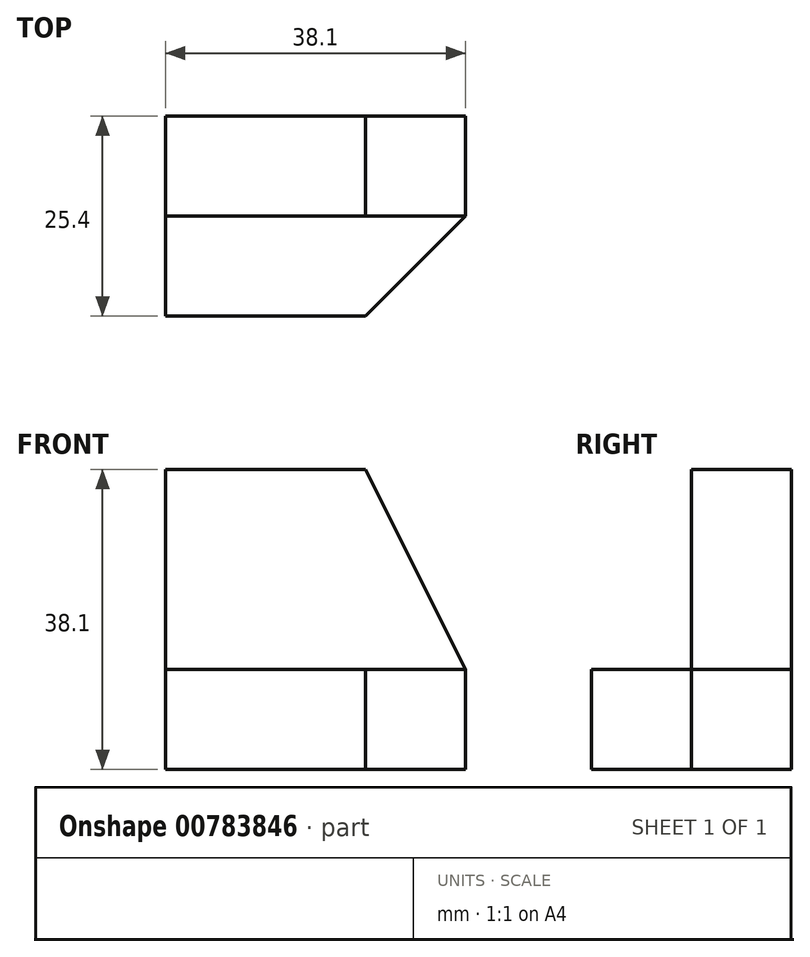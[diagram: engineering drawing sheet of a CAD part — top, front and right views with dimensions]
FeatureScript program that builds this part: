
annotation { "Feature Type Name" : "Feature", "Feature Type Description" : "" }
export const myFeature = defineFeature(function(context is Context, id is Id, definition is map)
    precondition{}
    {
        {
            var Q0;
            Q0=qCreatedBy(makeId("Front.planeOp"),FACE);
            var sketch = newSketch(context, id + "F0", { "sketchPlane" : qUnion([Q0])});
            skLineSegment(sketch, "E0", {"start": v(0, 0) * mm, "end": v(38.1, 0) * mm});
            skLineSegment(sketch, "E1", {"start": v(38.1, 0) * mm, "end": v(38.1, 38.1) * mm});
            skLineSegment(sketch, "E2", {"start": v(38.1, 38.1) * mm, "end": v(0, 38.1) * mm});
            skLineSegment(sketch, "E3", {"start": v(0, 38.1) * mm, "end": v(0, 0) * mm});
            skSolve(sketch);
        }
        {
            var Q0;
            Q0=makeQuery(id+"F0.imprint","IMPRINT",FACE,{"disambiguationData":[TD([[makeQuery(id+"F0.imprint","IMPRINT",EDGE,{"derivedFrom":sQuery(id+"F0.wireOp",EDGE,"E0")}),1.0]])]});
            extrude(context, id + "F1", {"entities" : qUnion([Q0]), "depth" : 25.4 * mm, "offsetDistance" : 25.4 * mm});
        }
        {
            var Q0;
            Q0=makeQuery(id+"F1.opExtrude","SWEPT_FACE",FACE,{"disambiguationData":[OSD([sQuery(id+"F0.wireOp",EDGE,"E1")])]});
            var sketch = newSketch(context, id + "F2", { "sketchPlane" : qUnion([Q0])});
            skLineSegment(sketch, "E4", {"start": v(-25.4, 0) * mm, "end": v(-25.4, 12.7) * mm});
            skLineSegment(sketch, "E5", {"start": v(-25.4, 12.7) * mm, "end": v(-12.7, 12.7) * mm});
            skLineSegment(sketch, "E6", {"start": v(-12.7, 12.7) * mm, "end": v(-12.7, 38.1) * mm});
            skLineSegment(sketch, "E7", {"start": v(-12.7, 38.1) * mm, "end": v(0, 38.1) * mm});
            skSolve(sketch);
        }
        {
            var Q0;
            Q0 = qSketchRegion(id + "F2", true);
            var Q1;
            {var subQ0=sQuery(id+"F2.wireOp",EDGE,"E5");Q1=makeQuery(id+"F2.imprint","IMPRINT",FACE,{"disambiguationData":[TD([[makeQuery(id+"F2.imprint","IMPRINT",EDGE,{"derivedFrom":subQ0}),1.0]])]});}
            extrude(context, id + "F3", {"entities" : qUnion([Q0, Q1]), "operationType" : NewBodyOperationType.REMOVE, "oppositeDirection" : true, "depth" : 38.1 * mm, "offsetDistance" : 25.4 * mm});
        }
        {
            var Q0;
            Q0=makeQuery(id+"F3.boolean.opBoolean","COPY",FACE,{"derivedFrom":makeQuery(id+"F3.opExtrude","SWEPT_FACE",FACE,{"disambiguationData":[OSD([sQuery(id+"F2.wireOp",EDGE,"E5")])]})});
            var sketch = newSketch(context, id + "F4", { "sketchPlane" : qUnion([Q0])});
            skLineSegment(sketch, "E8", {"start": v(38.1, -25.4) * mm, "end": v(25.4, -25.4) * mm});
            skLineSegment(sketch, "E9", {"start": v(25.4, -25.4) * mm, "end": v(38.1, -12.7) * mm});
            skSolve(sketch);
        }
        {
            var Q0;
            Q0 = qSketchRegion(id + "F4", true);
            var Q1;
            Q1=makeQuery(id+"F4.imprint","IMPRINT",FACE,{"disambiguationData":[TD([[makeQuery(id+"F4.imprint","IMPRINT",EDGE,{"derivedFrom":sQuery(id+"F4.wireOp",EDGE,"E8")}),1.0]])]});
            extrude(context, id + "F5", {"entities" : qUnion([Q0, Q1]), "operationType" : NewBodyOperationType.REMOVE, "oppositeDirection" : true, "depth" : 25.4 * mm, "offsetDistance" : 25.4 * mm});
        }
        {
            var Q0;
            Q0=makeQuery(id+"F3.boolean.opBoolean","COPY",FACE,{"derivedFrom":makeQuery(id+"F3.opExtrude","SWEPT_FACE",FACE,{"disambiguationData":[OSD([sQuery(id+"F2.wireOp",EDGE,"E6")])]})});
            var sketch = newSketch(context, id + "F6", { "sketchPlane" : qUnion([Q0])});
            skLineSegment(sketch, "E10", {"start": v(38.1, 38.1) * mm, "end": v(25.4, 38.1) * mm});
            skLineSegment(sketch, "E11", {"start": v(25.4, 38.1) * mm, "end": v(38.1, 12.7) * mm});
            skSolve(sketch);
        }
        {
            var Q0;
            Q0=makeQuery(id+"F6.imprint","IMPRINT",FACE,{"disambiguationData":[TD([[makeQuery(id+"F6.imprint","IMPRINT",EDGE,{"derivedFrom":sQuery(id+"F6.wireOp",EDGE,"E10")}),-1.0]])]});
            extrude(context, id + "F7", {"entities" : qUnion([Q0]), "operationType" : NewBodyOperationType.REMOVE, "oppositeDirection" : true, "depth" : 25.4 * mm, "offsetDistance" : 25.4 * mm});
        }
    });
